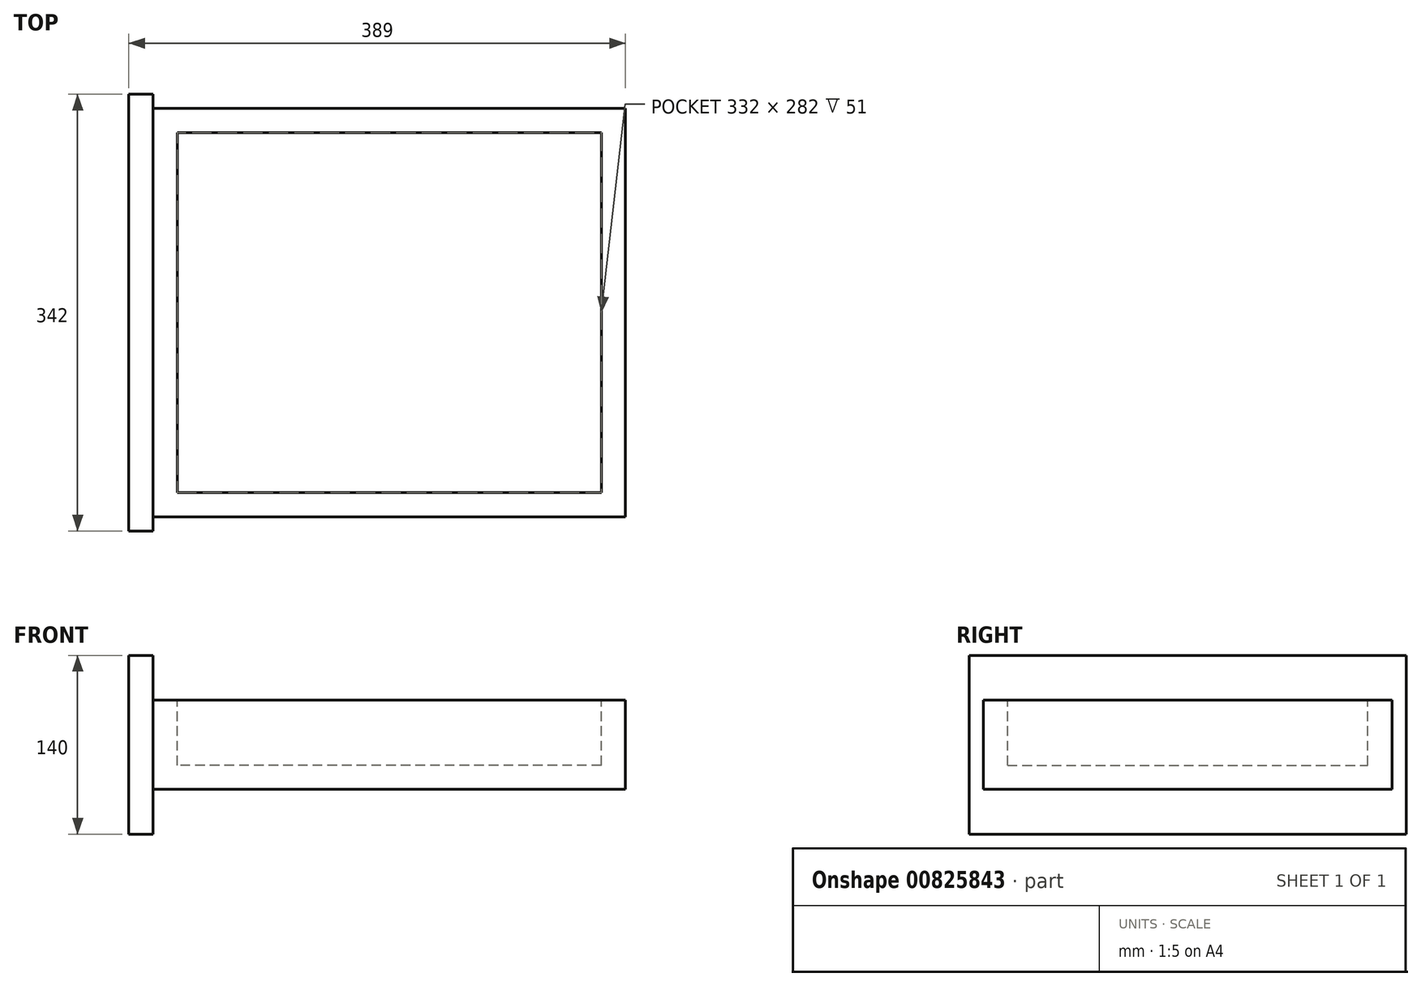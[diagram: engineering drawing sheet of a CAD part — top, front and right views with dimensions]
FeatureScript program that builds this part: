
annotation { "Feature Type Name" : "Feature", "Feature Type Description" : "" }
export const myFeature = defineFeature(function(context is Context, id is Id, definition is map)
    precondition{}
    {
        {
            var Q0;
            Q0=qCreatedBy(makeId("Top.planeOp"),FACE);
            var sketch = newSketch(context, id + "F0", { "sketchPlane" : qUnion([Q0])});
            skLineSegment(sketch, "E0.bottom", {"start": v(185, -160) * mm, "end": v(-185, -160) * mm});
            skLineSegment(sketch, "E0.top", {"start": v(185, 160) * mm, "end": v(-185, 160) * mm});
            skLineSegment(sketch, "E0.left", {"start": v(185, -160) * mm, "end": v(185, 160) * mm});
            skLineSegment(sketch, "E0.right", {"start": v(-185, -160) * mm, "end": v(-185, 160) * mm});
            skPoint(sketch, "E0.middle", {"position": v(0, 0) * mm});
            skSolve(sketch);
        }
        {
            var Q0;
            Q0=makeQuery(id+"F0.imprint","IMPRINT",FACE,{"disambiguationData":[TD([[makeQuery(id+"F0.imprint","IMPRINT",EDGE,{"derivedFrom":sQuery(id+"F0.wireOp",EDGE,"E0.bottom")}),-1.0]])]});
            extrude(context, id + "F1", {"entities" : qUnion([Q0]), "depth" : 70 * mm, "offsetDistance" : 25 * mm});
        }
        {
            var Q0;
            Q0=makeQuery(id+"F1.opExtrude","CAP_FACE",FACE,{"disambiguationData":[OSD([sQuery(id+"F0.wireOp",EDGE,"E0.bottom"),sQuery(id+"F0.wireOp",EDGE,"E0.top"),sQuery(id+"F0.wireOp",EDGE,"E0.left"),sQuery(id+"F0.wireOp",EDGE,"E0.right")])],"isStart":false});
            var sketch = newSketch(context, id + "F2", { "sketchPlane" : qUnion([Q0])});
            skLineSegment(sketch, "E1.bottom", {"start": v(166, -141) * mm, "end": v(-166, -141) * mm});
            skLineSegment(sketch, "E1.top", {"start": v(166, 141) * mm, "end": v(-166, 141) * mm});
            skLineSegment(sketch, "E1.left", {"start": v(166, -141) * mm, "end": v(166, 141) * mm});
            skLineSegment(sketch, "E1.right", {"start": v(-166, -141) * mm, "end": v(-166, 141) * mm});
            skPoint(sketch, "E1.middle", {"position": v(0, 0) * mm});
            skSolve(sketch);
        }
        {
            var Q0;
            Q0=makeQuery(id+"F2.imprint","IMPRINT",FACE,{"disambiguationData":[TD([[makeQuery(id+"F2.imprint","IMPRINT",EDGE,{"derivedFrom":sQuery(id+"F2.wireOp",EDGE,"E1.bottom")}),-1.0]])]});
            extrude(context, id + "F3", {"entities" : qUnion([Q0]), "operationType" : NewBodyOperationType.REMOVE, "oppositeDirection" : true, "depth" : 51 * mm, "offsetDistance" : 25 * mm});
        }
        {
            var Q0;
            Q0=makeQuery(id+"F1.opExtrude","SWEPT_FACE",FACE,{"disambiguationData":[OSD([sQuery(id+"F0.wireOp",EDGE,"E0.right")])]});
            var sketch = newSketch(context, id + "F4", { "sketchPlane" : qUnion([Q0])});
            skLineSegment(sketch, "E2.bottom", {"start": v(171, -35) * mm, "end": v(-171, -35) * mm});
            skLineSegment(sketch, "E2.top", {"start": v(171, 105) * mm, "end": v(-171, 105) * mm});
            skLineSegment(sketch, "E2.left", {"start": v(171, -35) * mm, "end": v(171, 105) * mm});
            skLineSegment(sketch, "E2.right", {"start": v(-171, -35) * mm, "end": v(-171, 105) * mm});
            skPoint(sketch, "E2.middle", {"position": v(0, 35) * mm});
            skPoint(sketch, "E2.middle.positionSnap0", {"position": v(160, 35) * mm});
            skPoint(sketch, "E2.middle.positionSnap1", {"position": v(0, 0) * mm});
            skPoint(sketch, "E2.centerSnap0", {"position": v(160, 35) * mm});
            skPoint(sketch, "E2.centerSnap1", {"position": v(0, 0) * mm});
            skSolve(sketch);
        }
        {
            var Q0;
            Q0 = qSketchRegion(id + "F4", true);
            extrude(context, id + "F5", {"entities" : qUnion([Q0]), "operationType" : NewBodyOperationType.ADD, "depth" : 19 * mm, "offsetDistance" : 25 * mm});
        }
    });
